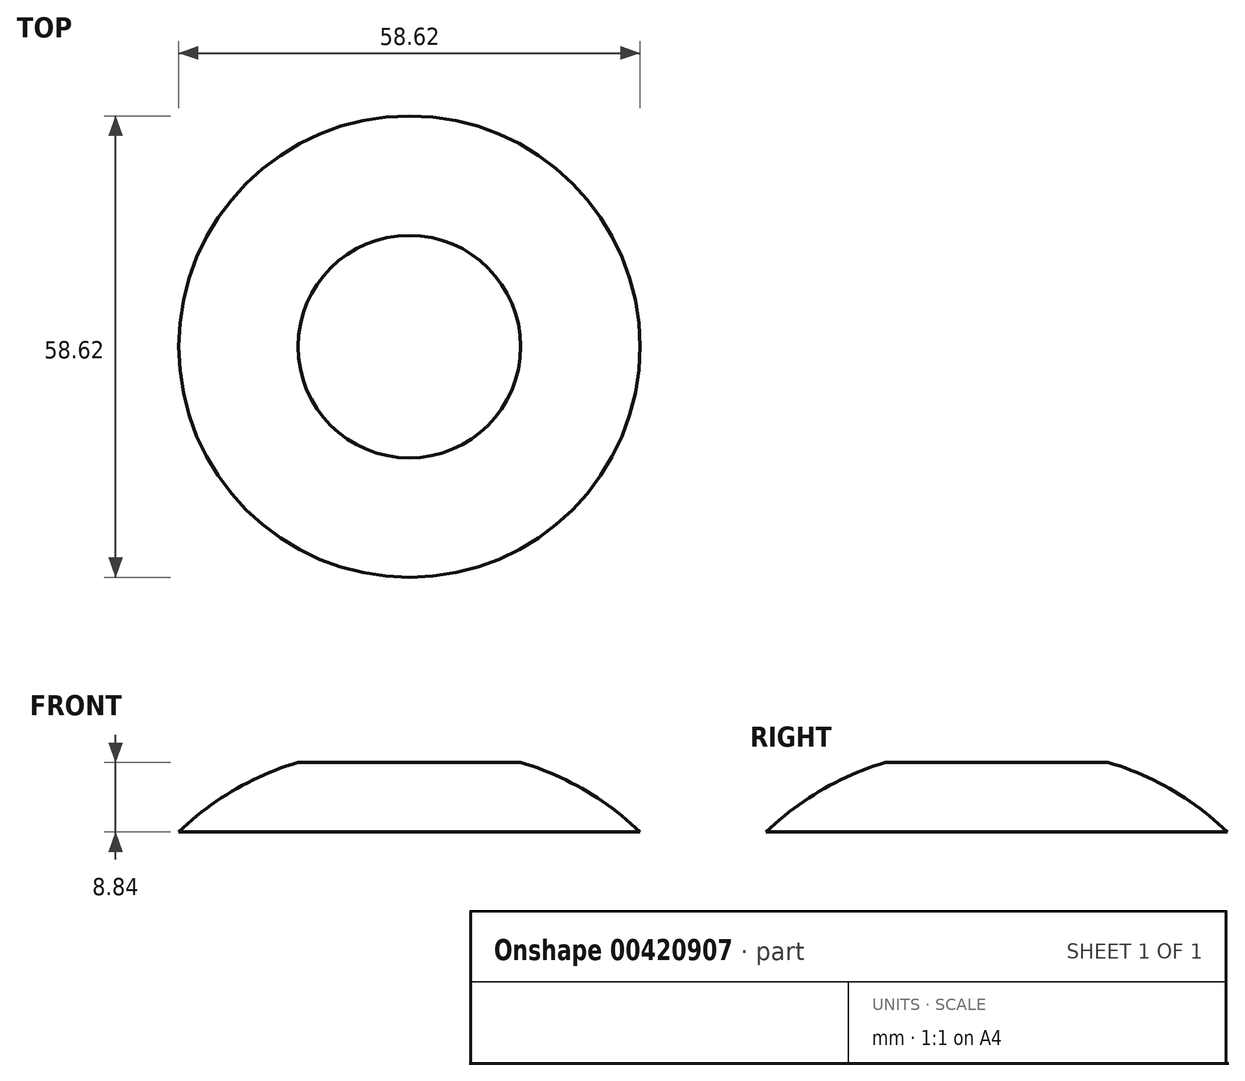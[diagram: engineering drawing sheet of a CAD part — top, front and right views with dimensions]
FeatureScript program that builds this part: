
annotation { "Feature Type Name" : "Feature", "Feature Type Description" : "" }
export const myFeature = defineFeature(function(context is Context, id is Id, definition is map)
    precondition{}
    {
        {
            var Q0;
            Q0=qCreatedBy(makeId("Front.planeOp"),FACE);
            var sketch = newSketch(context, id + "F0", { "sketchPlane" : qUnion([Q0])});
            skLineSegment(sketch, "E0", {"start": v(0, 0) * mm, "end": v(0, 8.84) * mm});
            skArc(sketch, "E1", {"start": v(29.3, 0) * mm, "mid": v(22.25, 5.32) * mm, "end": v(14.14, 8.84) * mm});
            skLineSegment(sketch, "E2", {"start": v(0, 0) * mm, "end": v(29.3, 0) * mm});
            skLineSegment(sketch, "E3", {"start": v(0, 8.84) * mm, "end": v(14.14, 8.84) * mm});
            skSolve(sketch);
        }
        {
            var Q0;
            Q0=makeQuery(id+"F0.imprint","IMPRINT",FACE,{"disambiguationData":[TD([[makeQuery(id+"F0.imprint","IMPRINT",EDGE,{"derivedFrom":sQuery(id+"F0.wireOp",EDGE,"E0")}),-1.0]])]});
            var Q1;
            Q1=sQuery(id+"F0.wireOp",EDGE,"E0");
            revolve(context, id + "F1", {"entities" : qUnion([Q0]), "axis" : qUnion([Q1]), "revolveType" : RevolveType.FULL});
        }
    });
